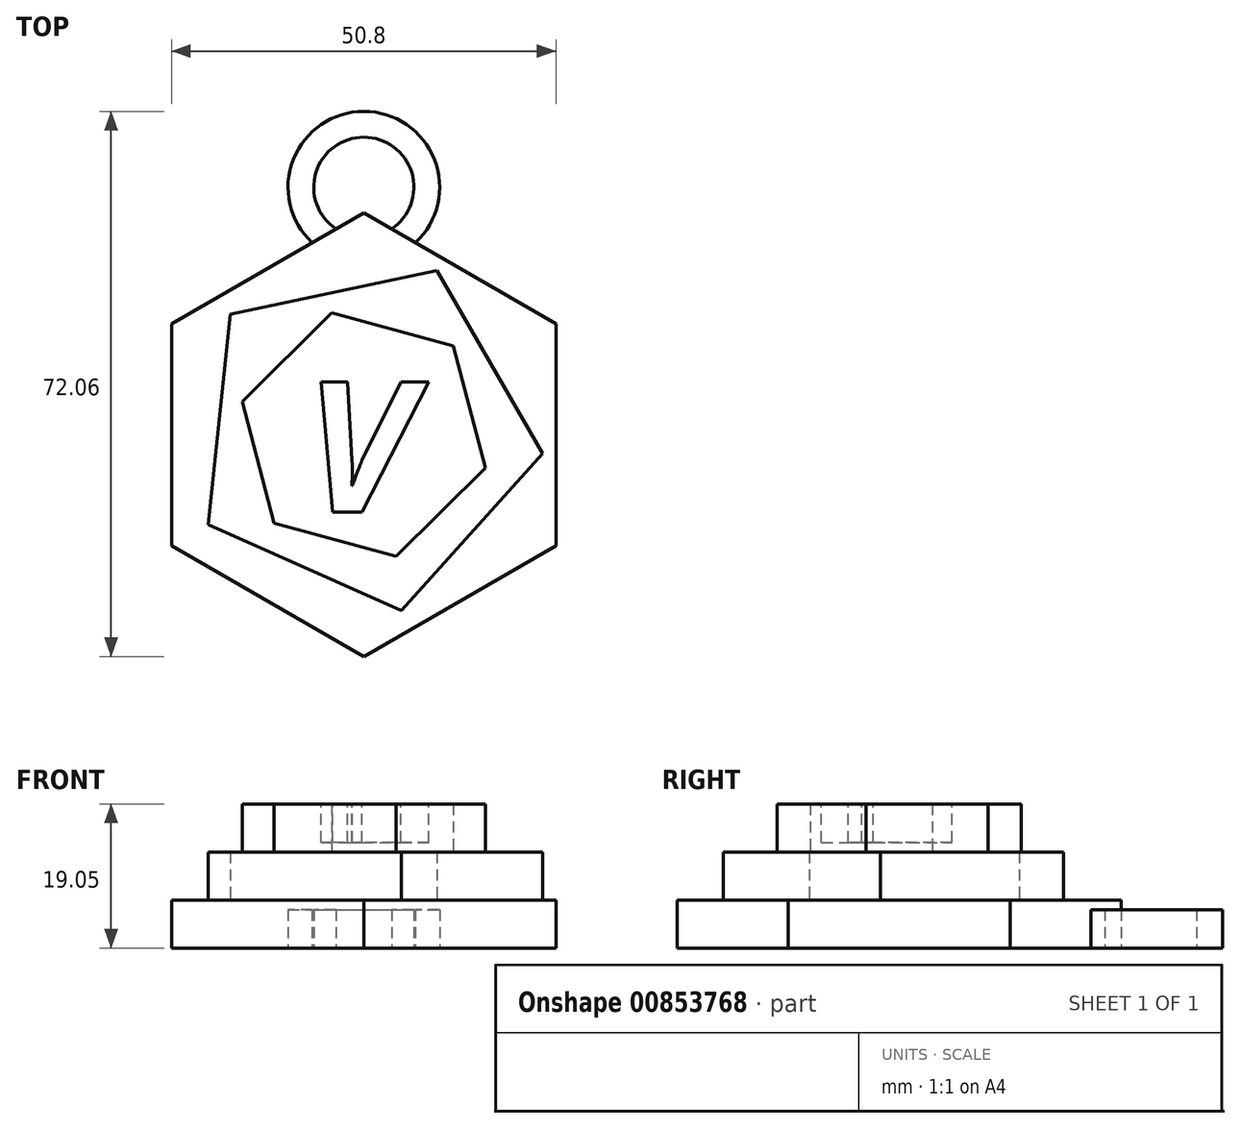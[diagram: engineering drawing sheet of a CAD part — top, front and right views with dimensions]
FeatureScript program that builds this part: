
annotation { "Feature Type Name" : "Feature", "Feature Type Description" : "" }
export const myFeature = defineFeature(function(context is Context, id is Id, definition is map)
    precondition{}
    {
        {
            var Q0;
            Q0=qCreatedBy(makeId("Top.planeOp"),FACE);
            var sketch = newSketch(context, id + "F0", { "sketchPlane" : qUnion([Q0])});
            skCircle(sketch, "E0.cCircle", {"center": v(0, 0) * mm, "radius": 25.4 * mm, "construction": true});
            skLineSegment(sketch, "E0.0", {"start": v(25.4, 14.66) * mm, "end": v(25.4, -14.66) * mm});
            skLineSegment(sketch, "E0.1", {"start": v(25.4, -14.66) * mm, "end": v(0, -29.33) * mm});
            skLineSegment(sketch, "E0.2", {"start": v(0, -29.33) * mm, "end": v(-25.4, -14.66) * mm});
            skLineSegment(sketch, "E0.3", {"start": v(-25.4, -14.66) * mm, "end": v(-25.4, 14.66) * mm});
            skLineSegment(sketch, "E0.4", {"start": v(-25.4, 14.66) * mm, "end": v(0, 29.33) * mm});
            skLineSegment(sketch, "E0.5", {"start": v(0, 29.33) * mm, "end": v(25.4, 14.66) * mm});
            skPoint(sketch, "E0.0.midPoint", {"position": v(25.4, 0) * mm});
            skSolve(sketch);
        }
        {
            var Q0;
            Q0=makeQuery(id+"F0.imprint","IMPRINT",FACE,{"disambiguationData":[TD([[makeQuery(id+"F0.imprint","IMPRINT",EDGE,{"derivedFrom":sQuery(id+"F0.wireOp",EDGE,"E0.0")}),-1.0]])]});
            extrude(context, id + "F1", {"entities" : qUnion([Q0]), "depth" : 6.35 * mm, "offsetDistance" : 25.4 * mm});
        }
        {
            var Q0;
            Q0=makeQuery(id+"F1.opExtrude","CAP_FACE",FACE,{"disambiguationData":[OSD([sQuery(id+"F0.wireOp",EDGE,"E0.0"),sQuery(id+"F0.wireOp",EDGE,"E0.1"),sQuery(id+"F0.wireOp",EDGE,"E0.2"),sQuery(id+"F0.wireOp",EDGE,"E0.3"),sQuery(id+"F0.wireOp",EDGE,"E0.4"),sQuery(id+"F0.wireOp",EDGE,"E0.5")])],"isStart":false});
            var sketch = newSketch(context, id + "F2", { "sketchPlane" : qUnion([Q0])});
            skCircle(sketch, "E1.cCircle", {"center": v(0, 0) * mm, "radius": 19.23 * mm, "construction": true});
            skLineSegment(sketch, "E1.0", {"start": v(9.67, 21.71) * mm, "end": v(23.64, -2.48) * mm});
            skLineSegment(sketch, "E1.1", {"start": v(23.64, -2.48) * mm, "end": v(4.94, -23.25) * mm});
            skLineSegment(sketch, "E1.2", {"start": v(4.94, -23.25) * mm, "end": v(-20.58, -11.88) * mm});
            skLineSegment(sketch, "E1.3", {"start": v(-20.58, -11.88) * mm, "end": v(-17.66, 15.9) * mm});
            skLineSegment(sketch, "E1.4", {"start": v(-17.66, 15.9) * mm, "end": v(9.67, 21.71) * mm});
            skPoint(sketch, "E1.0.midPoint", {"position": v(16.65, 9.61) * mm});
            skSolve(sketch);
        }
        {
            var Q0;
            Q0 = qSketchRegion(id + "F2", true);
            extrude(context, id + "F3", {"entities" : qUnion([Q0]), "operationType" : NewBodyOperationType.ADD, "depth" : 6.35 * mm, "offsetDistance" : 25.4 * mm});
        }
        {
            var Q0;
            Q0=makeQuery(id+"F3.opExtrude","CAP_FACE",FACE,{"disambiguationData":[OSD([sQuery(id+"F2.wireOp",EDGE,"E1.0"),sQuery(id+"F2.wireOp",EDGE,"E1.1"),sQuery(id+"F2.wireOp",EDGE,"E1.2"),sQuery(id+"F2.wireOp",EDGE,"E1.3"),sQuery(id+"F2.wireOp",EDGE,"E1.4")])],"isStart":false});
            var sketch = newSketch(context, id + "F4", { "sketchPlane" : qUnion([Q0])});
            skSolve(sketch);
        }
        {
            var Q0;
            Q0=makeQuery(id+"F4.imprint","IMPRINT",FACE,{"disambiguationData":[TD([[makeQuery(id+"F4.imprint","IMPRINT",EDGE,{"derivedFrom":makeQuery(id+"F3.opExtrude","CAP_EDGE",EDGE,{"disambiguationData":[OSD([sQuery(id+"F2.wireOp",EDGE,"E1.0")])],"isStart":false})}),-1.0]])]});
            var sketch = newSketch(context, id + "F5", { "sketchPlane" : qUnion([Q0])});
            skCircle(sketch, "E2.cCircle", {"center": v(0, 0) * mm, "radius": 14.43 * mm, "construction": true});
            skLineSegment(sketch, "E2.0", {"start": v(16.08, -4.38) * mm, "end": v(4.25, -16.12) * mm});
            skLineSegment(sketch, "E2.1", {"start": v(4.25, -16.12) * mm, "end": v(-11.83, -11.74) * mm});
            skLineSegment(sketch, "E2.2", {"start": v(-11.83, -11.74) * mm, "end": v(-16.08, 4.38) * mm});
            skLineSegment(sketch, "E2.3", {"start": v(-16.08, 4.38) * mm, "end": v(-4.25, 16.12) * mm});
            skLineSegment(sketch, "E2.4", {"start": v(-4.25, 16.12) * mm, "end": v(11.83, 11.74) * mm});
            skLineSegment(sketch, "E2.5", {"start": v(11.83, 11.74) * mm, "end": v(16.08, -4.38) * mm});
            skPoint(sketch, "E2.0.midPoint", {"position": v(10.16, -10.25) * mm});
            skSolve(sketch);
        }
        {
            var Q0;
            Q0 = qSketchRegion(id + "F5", true);
            extrude(context, id + "F6", {"entities" : qUnion([Q0]), "operationType" : NewBodyOperationType.ADD, "depth" : 6.35 * mm, "offsetDistance" : 25.4 * mm});
        }
        {
            var Q0;
            Q0=makeQuery(id+"F6.opExtrude","CAP_FACE",FACE,{"disambiguationData":[OSD([sQuery(id+"F5.wireOp",EDGE,"E2.0"),sQuery(id+"F5.wireOp",EDGE,"E2.1"),sQuery(id+"F5.wireOp",EDGE,"E2.2"),sQuery(id+"F5.wireOp",EDGE,"E2.3"),sQuery(id+"F5.wireOp",EDGE,"E2.4"),sQuery(id+"F5.wireOp",EDGE,"E2.5")])],"isStart":false});
            var sketch = newSketch(context, id + "F7", { "sketchPlane" : qUnion([Q0])});
            skText(sketch, "E3", { "text": "V", "fontName": "OpenSans-BoldItalic.ttf"});
            const initialGuessF7  = {"E3": [-0.00781, -0.01025, 1, 0, 0.01737]};
            skSetInitialGuess(sketch, initialGuessF7);
            skSolve(sketch);
        }
        {
            var Q0;
            Q0=makeQuery(id+"F7.imprint","IMPRINT",FACE,{"disambiguationData":[TD([[makeQuery(id+"F7.imprint","IMPRINT",EDGE,{"derivedFrom":sQuery(id+"F7.wireOp",EDGE,"E3.sketch_text.stroke-0")}),-1.0]])]});
            extrude(context, id + "F8", {"entities" : qUnion([Q0]), "operationType" : NewBodyOperationType.REMOVE, "oppositeDirection" : true, "depth" : 5.08 * mm, "offsetDistance" : 25.4 * mm});
        }
        {
            var Q0;
            Q0=makeQuery(id+"F1.opExtrude","CAP_FACE",FACE,{"disambiguationData":[OSD([sQuery(id+"F0.wireOp",EDGE,"E0.0"),sQuery(id+"F0.wireOp",EDGE,"E0.1"),sQuery(id+"F0.wireOp",EDGE,"E0.2"),sQuery(id+"F0.wireOp",EDGE,"E0.3"),sQuery(id+"F0.wireOp",EDGE,"E0.4"),sQuery(id+"F0.wireOp",EDGE,"E0.5")])],"isStart":true});
            var sketch = newSketch(context, id + "F9", { "sketchPlane" : qUnion([Q0])});
            skCircle(sketch, "E4", {"center": v(0, -32.71) * mm, "radius": 10.02 * mm});
            skCircle(sketch, "E5", {"center": v(0, -32.71) * mm, "radius": 6.62 * mm});
            skSolve(sketch);
        }
        {
            var Q0;
            {var subQ0=sQuery(id+"F9.wireOp",EDGE,"E4");var subQ1=makeQuery(id+"F1.opExtrude","CAP_EDGE",EDGE,{"disambiguationData":[OSD([sQuery(id+"F0.wireOp",EDGE,"E0.4")])],"isStart":true});var subQ2=makeQuery(id+"F9.imprint","INTERSECT",VERTEX,{"derivedFrom":[subQ1,subQ0]});Q0=makeQuery(id+"F9.imprint","IMPRINT",FACE,{"disambiguationData":[TD([[makeQuery(id+"F9.imprint","IMPRINT",EDGE,{"disambiguationData":[TD([[subQ2,-1.0]])],"derivedFrom":subQ0}),1.0]])]});}
            extrude(context, id + "F10", {"entities" : qUnion([Q0]), "operationType" : NewBodyOperationType.ADD, "oppositeDirection" : true, "depth" : 5.08 * mm, "offsetDistance" : 25.4 * mm});
        }
    });
